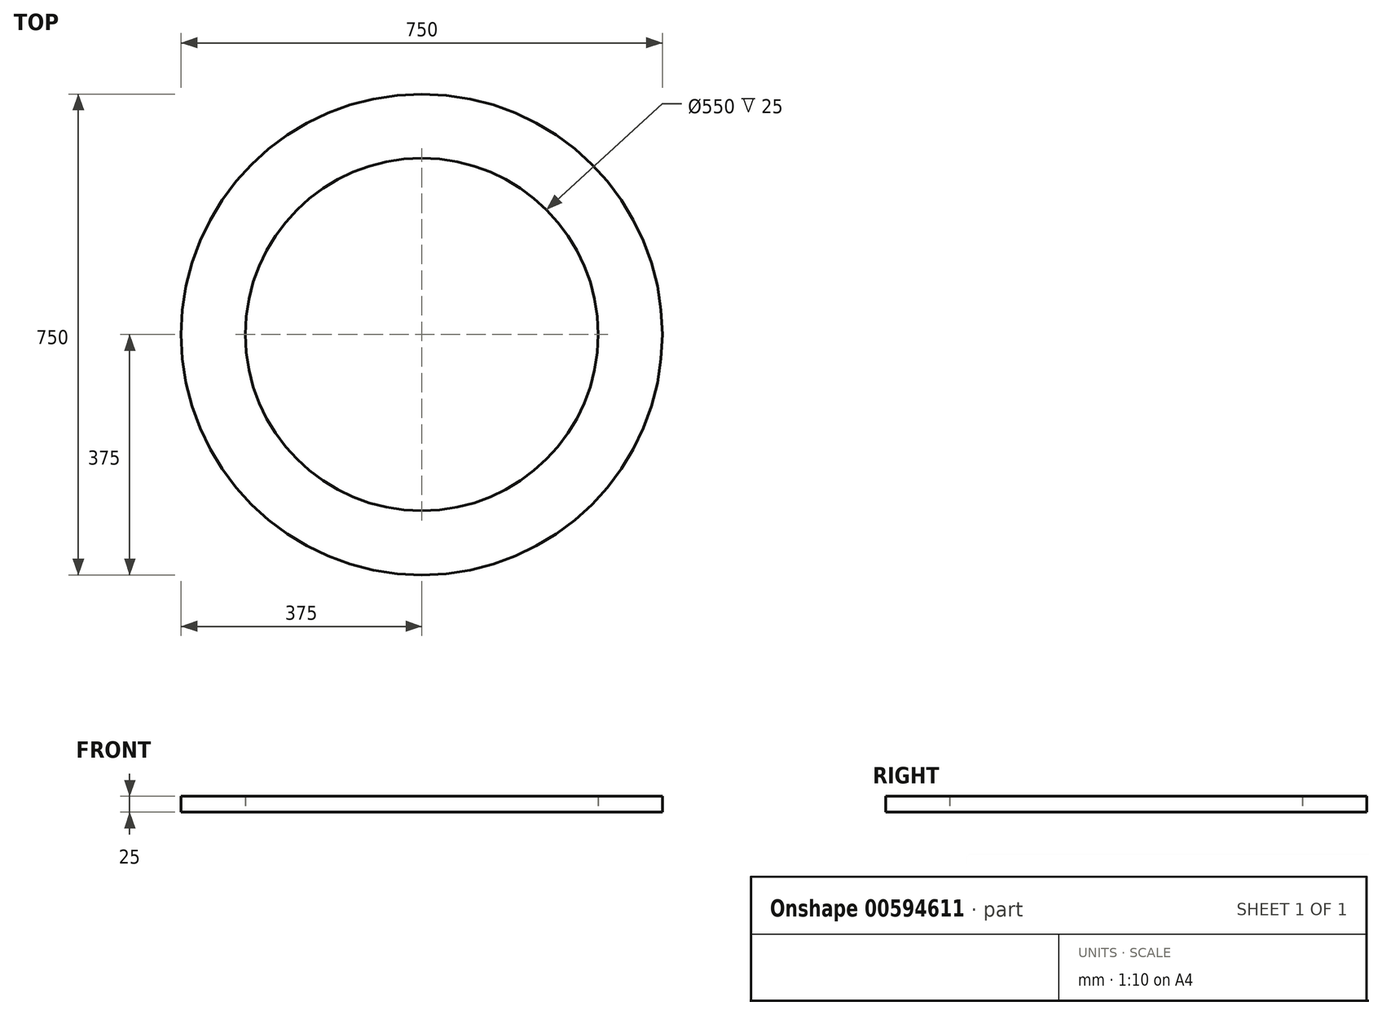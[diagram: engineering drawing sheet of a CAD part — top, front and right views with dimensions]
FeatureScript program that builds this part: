
annotation { "Feature Type Name" : "Feature", "Feature Type Description" : "" }
export const myFeature = defineFeature(function(context is Context, id is Id, definition is map)
    precondition{}
    {
        {
            var Q0;
            Q0=qCreatedBy(makeId("Top.planeOp"),FACE);
            var sketch = newSketch(context, id + "F0", { "sketchPlane" : qUnion([Q0])});
            skCircle(sketch, "E0", {"center": v(0, 0) * mm, "radius": 275 * mm});
            skCircle(sketch, "E1", {"center": v(0, 0) * mm, "radius": 375 * mm});
            skSolve(sketch);
        }
        {
            var Q0;
            Q0=makeQuery(id+"F0.imprint","IMPRINT",FACE,{"disambiguationData":[TD([[makeQuery(id+"F0.imprint","IMPRINT",EDGE,{"derivedFrom":sQuery(id+"F0.wireOp",EDGE,"E0")}),-1.0]])]});
            extrude(context, id + "F1", {"entities" : qUnion([Q0]), "depth" : 25 * mm, "offsetDistance" : 25 * mm});
        }
    });
